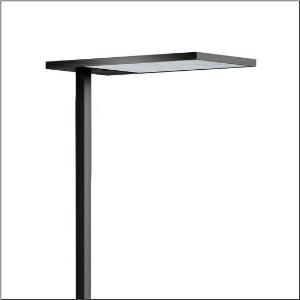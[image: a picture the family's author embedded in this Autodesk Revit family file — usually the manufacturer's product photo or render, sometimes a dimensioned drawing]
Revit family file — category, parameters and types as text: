
# Revit family: silica_r__21_floor_r_51mx53sg4db_4ec3
name_source: partatom
category: Lighting Fixtures
units: mm (PartAtom-declared; Revit-internal decimal feet)

## family parameters
Cut with Voids When Loaded = No
Host = Face
Light Source = No
Part Type = Normal
Room Calculation Point = No
Round Connector Dimension = Use Diameter
Shared = No

## types (1)
- Silica® 21 Floor R (1 x LED, 15000 lm, 106.4 W, 4000K)
    Apparent Load = 106 VA
    CIE Flux Codes = 54 86 97 13 100
    Color Rendering = 80
    Color Temperature = 4000K
    Default Elevation = 1800 mm
    Description = Silica® 21 Floor R, floorstanding luminaire, of PMMA, primary optical cover: prismatic diffuser, of PMMA, CAT 2 (L<= 3000cd/m²), light emission: indirect/direct distribution, primary light characteristic: symmetric, primary optical cover: cover panel, of PMMA, installation type: not mounted, LED, rated luminous flux: 15.000lm, luminous efficacy: 141lm/W, light colour: 840, colour temperature: 4000K, control gear: DALI 2, daylight-dependent control, mains connection: 230V, AC, 50/60Hz, connection cable pre-assembled, cable length: 2,5m, rated input power: 106.4W, luminaire head, of aluminium, coated, jet black (RAL 9005), length: 671mm, width: 330mm, height: 2010mm, supporting column, angular, of aluminium, coated, jet black (RAL 9005), baseplate, of steel, coated, jet black (RAL 9005), protection rating (complete): IP20, insulation class (complete): insulation class I (protective earthing), certification: CE, standard: EN 50419, packaging unit: 1 piece
    Height = 18 mm
    Lamp = 1 x LED
    Lamp Light Flux = 15000 lm
    Lamp Power = 106.4 W
    Lamp count = 1
    Length = 650 mm
    Luminous efficacy = 141 lm/W
    Manufacturer = Siteco
    ModVariant = No
    Model = 51MX53SG4DB
    Mounting Place = Floor
    Mounting Type = Freestanding
    Number of Poles = 1
    OnlyDefault = Yes
    Power Factor = 1
    Product Name = Silica® 21 Floor R
    Product group = floorstanding luminaire
    ProductGroupID = 1302
    Protection Class = Protection class I
    Protection Degree = IP 20
    RLX_Detail_Level = 1
    RLX_Emergency_Light_Flux = 0 lm
    RLX_Emergency_Type = 0
    RLX_Emergency_Type_DB = No
    RlxData = <blob elided: 22057 chars, md5=08b857d5>
    Socket = socket
    Standby Power = 0 W
    System Light Flux = 15000 lm
    System Power = 106 W
    Type Comments = Product without accessories
    Type Image = l_1007011.jpg
    URL = http://relux.com
    VarID = ---
    Voltage = 0 V
    Weight = 0.00 kg
    Width = 350 mm

## geometry (parser evidence)
native form markers: Blend x4, Sweep x13
no freeform markers — native parametric forms only
